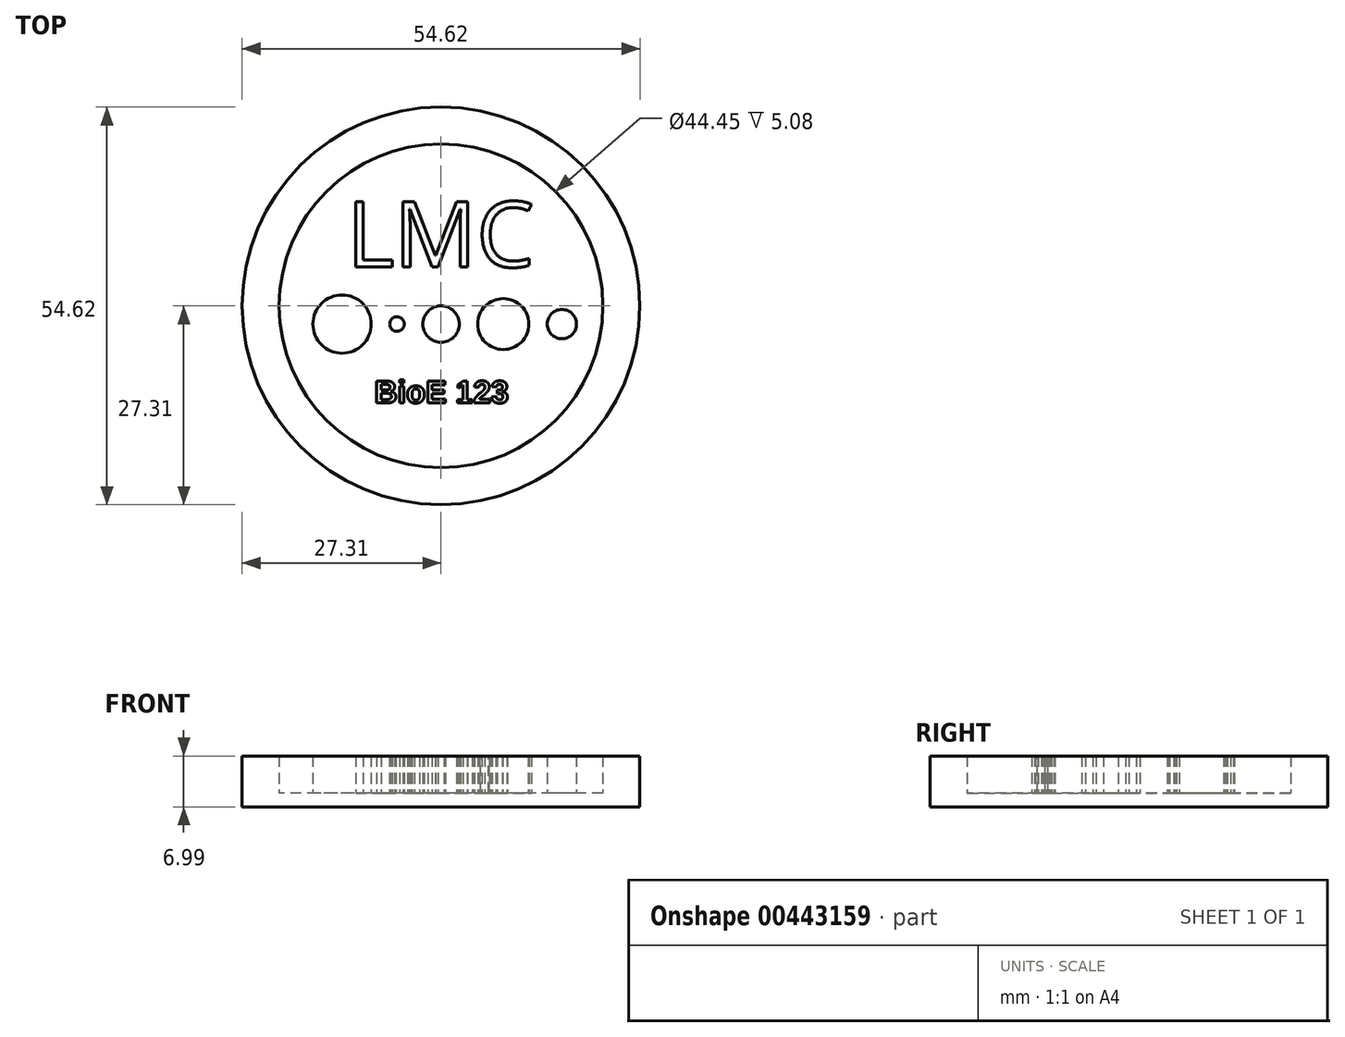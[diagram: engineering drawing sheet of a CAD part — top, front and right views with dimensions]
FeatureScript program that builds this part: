
annotation { "Feature Type Name" : "Feature", "Feature Type Description" : "" }
export const myFeature = defineFeature(function(context is Context, id is Id, definition is map)
    precondition{}
    {
        {
            var Q0;
            Q0=qCreatedBy(makeId("Top.planeOp"),FACE);
            var sketch = newSketch(context, id + "F0", { "sketchPlane" : qUnion([Q0])});
            skCircle(sketch, "E0", {"center": v(0, 0) * mm, "radius": 27.3 * mm});
            skCircle(sketch, "E1", {"center": v(0, 0) * mm, "radius": 22.23 * mm});
            skSolve(sketch);
        }
        {
            var Q0;
            Q0=makeQuery(id+"F0.imprint","IMPRINT",FACE,{"disambiguationData":[TD([[makeQuery(id+"F0.imprint","IMPRINT",EDGE,{"derivedFrom":sQuery(id+"F0.wireOp",EDGE,"E1")}),1.0]])]});
            extrude(context, id + "F1", {"entities" : qUnion([Q0]), "depth" : 1.9 * mm});
        }
        {
            var Q0;
            Q0=makeQuery(id+"F0.imprint","IMPRINT",FACE,{"disambiguationData":[TD([[makeQuery(id+"F0.imprint","IMPRINT",EDGE,{"derivedFrom":sQuery(id+"F0.wireOp",EDGE,"E0")}),1.0]])]});
            extrude(context, id + "F2", {"entities" : qUnion([Q0]), "operationType" : NewBodyOperationType.ADD, "depth" : 7 * mm});
        }
        {
            var Q0;
            Q0=qCreatedBy(makeId("Top.planeOp"),FACE);
            var sketch = newSketch(context, id + "F3", { "sketchPlane" : qUnion([Q0])});
            skCircle(sketch, "E2", {"center": v(-13.59, -2.5) * mm, "radius": 4 * mm});
            skCircle(sketch, "E3", {"center": v(-6.05, -2.5) * mm, "radius": 1 * mm});
            skCircle(sketch, "E4", {"center": v(0, -2.5) * mm, "radius": 2.5 * mm});
            skCircle(sketch, "E5", {"center": v(8.55, -2.5) * mm, "radius": 3.5 * mm});
            skCircle(sketch, "E6", {"center": v(16.6, -2.5) * mm, "radius": 2 * mm});
            skSolve(sketch);
        }
        {
            var Q0;
            Q0 = qSketchRegion(id + "F3", true);
            extrude(context, id + "F4", {"entities" : qUnion([Q0]), "operationType" : NewBodyOperationType.ADD, "depth" : 7 * mm});
        }
        {
            var Q0;
            Q0=qCreatedBy(makeId("Top.planeOp"),FACE);
            var sketch = newSketch(context, id + "F5", { "sketchPlane" : qUnion([Q0])});
            skText(sketch, "E7", { "text": "LMC", "fontName": "OpenSans-Regular.ttf"});
            const initialGuessF5  = {"E7": [-0.01295, 0.00535, 1, 0, 0.00903]};
            skSetInitialGuess(sketch, initialGuessF5);
            skSolve(sketch);
        }
        {
            var Q0;
            Q0 = qSketchRegion(id + "F5", true);
            extrude(context, id + "F6", {"entities" : qUnion([Q0]), "operationType" : NewBodyOperationType.ADD, "depth" : 7 * mm});
        }
        {
            var Q0;
            Q0=qCreatedBy(makeId("Top.planeOp"),FACE);
            var sketch = newSketch(context, id + "F7", { "sketchPlane" : qUnion([Q0])});
            skText(sketch, "E8", { "text": "BioE 123", "fontName": "Arimo-Bold.ttf"});
            const initialGuessF7  = {"E8": [-0.00915, -0.01333, 1, 0, 0.00314]};
            skSetInitialGuess(sketch, initialGuessF7);
            skSolve(sketch);
        }
        {
            var Q0;
            Q0 = qSketchRegion(id + "F7", true);
            extrude(context, id + "F8", {"entities" : qUnion([Q0]), "operationType" : NewBodyOperationType.ADD, "depth" : 7 * mm});
        }
    });
